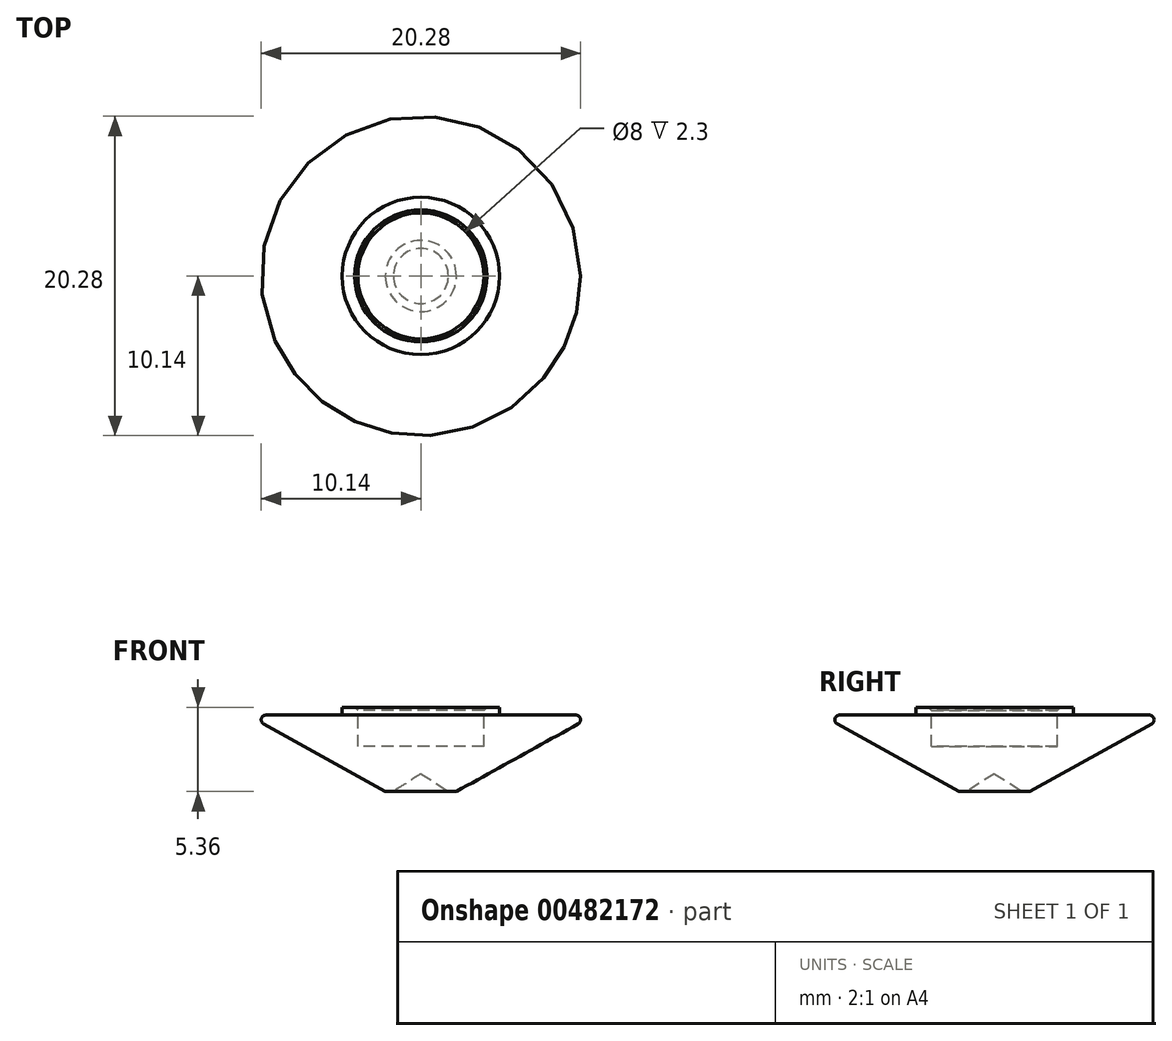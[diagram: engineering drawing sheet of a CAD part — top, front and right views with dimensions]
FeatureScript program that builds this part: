
annotation { "Feature Type Name" : "Feature", "Feature Type Description" : "" }
export const myFeature = defineFeature(function(context is Context, id is Id, definition is map)
    precondition{}
    {
        {
            var Q0;
            Q0=qCreatedBy(makeId("Front.planeOp"),FACE);
            var sketch = newSketch(context, id + "F0", { "sketchPlane" : qUnion([Q0])});
            skLineSegment(sketch, "E0", {"start": v(0, 0) * mm, "end": v(-11, 0) * mm});
            skLineSegment(sketch, "E1", {"start": v(0, 0) * mm, "end": v(0, -3.73) * mm});
            skLineSegment(sketch, "E2", {"start": v(0, -3.73) * mm, "end": v(-2, -5) * mm});
            skLineSegment(sketch, "E3", {"start": v(-2, -5) * mm, "end": v(-11, 0) * mm});
            skLineSegment(sketch, "E4.bottom", {"start": v(0, 0) * mm, "end": v(-4, 0) * mm});
            skLineSegment(sketch, "E4.top", {"start": v(0, -2) * mm, "end": v(-4, -2) * mm});
            skLineSegment(sketch, "E4.left", {"start": v(0, 0) * mm, "end": v(0, -2) * mm});
            skLineSegment(sketch, "E4.right", {"start": v(-4, 0) * mm, "end": v(-4, -2) * mm});
            skLineSegment(sketch, "E5", {"start": v(-4, 0) * mm, "end": v(-4, 0.5) * mm});
            skLineSegment(sketch, "E6", {"start": v(-4, 0.5) * mm, "end": v(-5, 0.5) * mm});
            skLineSegment(sketch, "E7", {"start": v(-5, 0.5) * mm, "end": v(-5, 0) * mm});
            skSolve(sketch);
        }
        {
            var Q0;
            Q0=makeQuery(id+"F0.imprint","IMPRINT",FACE,{"disambiguationData":[TD([[makeQuery(id+"F0.imprint","IMPRINT",EDGE,{"derivedFrom":sQuery(id+"F0.wireOp",EDGE,"E0")}),1.0]])]});
            var Q1;
            {var subQ0=sQuery(id+"F0.wireOp",EDGE,"E5");Q1=makeQuery(id+"F0.imprint","IMPRINT",FACE,{"disambiguationData":[TD([[makeQuery(id+"F0.imprint","IMPRINT",EDGE,{"derivedFrom":subQ0}),1.0]])]});}
            var Q2;
            Q2=sQuery(id+"F0.wireOp",EDGE,"E1");
            revolve(context, id + "F1", {"entities" : qUnion([Q0, Q1]), "axis" : qUnion([Q2]), "revolveType" : RevolveType.FULL});
        }
        {
            var Q0;
            Q0=makeQuery(id+"F1.opRevolve","SWEPT_EDGE",EDGE,{"disambiguationData":[OSD([sQuery(id+"F0.wireOp",EDGE,"E0"),sQuery(id+"F0.wireOp",EDGE,"E3")])]});
            fillet(context, id + "F2", {"entities" : qUnion([Q0]), "radius" : .3 * mm, "tangentPropagation" : true, "allowEdgeOverflow" : false});
        }
        {
            var Q0;
            Q0=makeQuery(id+"F1.opRevolve","SWEPT_EDGE",EDGE,{"disambiguationData":[OSD([sQuery(id+"F0.wireOp",EDGE,"E2"),sQuery(id+"F0.wireOp",EDGE,"E3")])]});
            chamfer(context, id + "F3", {"entities" : qUnion([Q0]), "width" : .5 * mm, "tangentPropagation" : true});
        }
        {
            var Q0;
            Q0=makeQuery(id+"F1.opRevolve","SWEPT_EDGE",EDGE,{"disambiguationData":[OSD([sQuery(id+"F0.wireOp",EDGE,"E5"),sQuery(id+"F0.wireOp",EDGE,"E6")])]});
            chamfer(context, id + "F4", {"entities" : qUnion([Q0]), "width" : .2 * mm, "tangentPropagation" : true});
        }
    });
